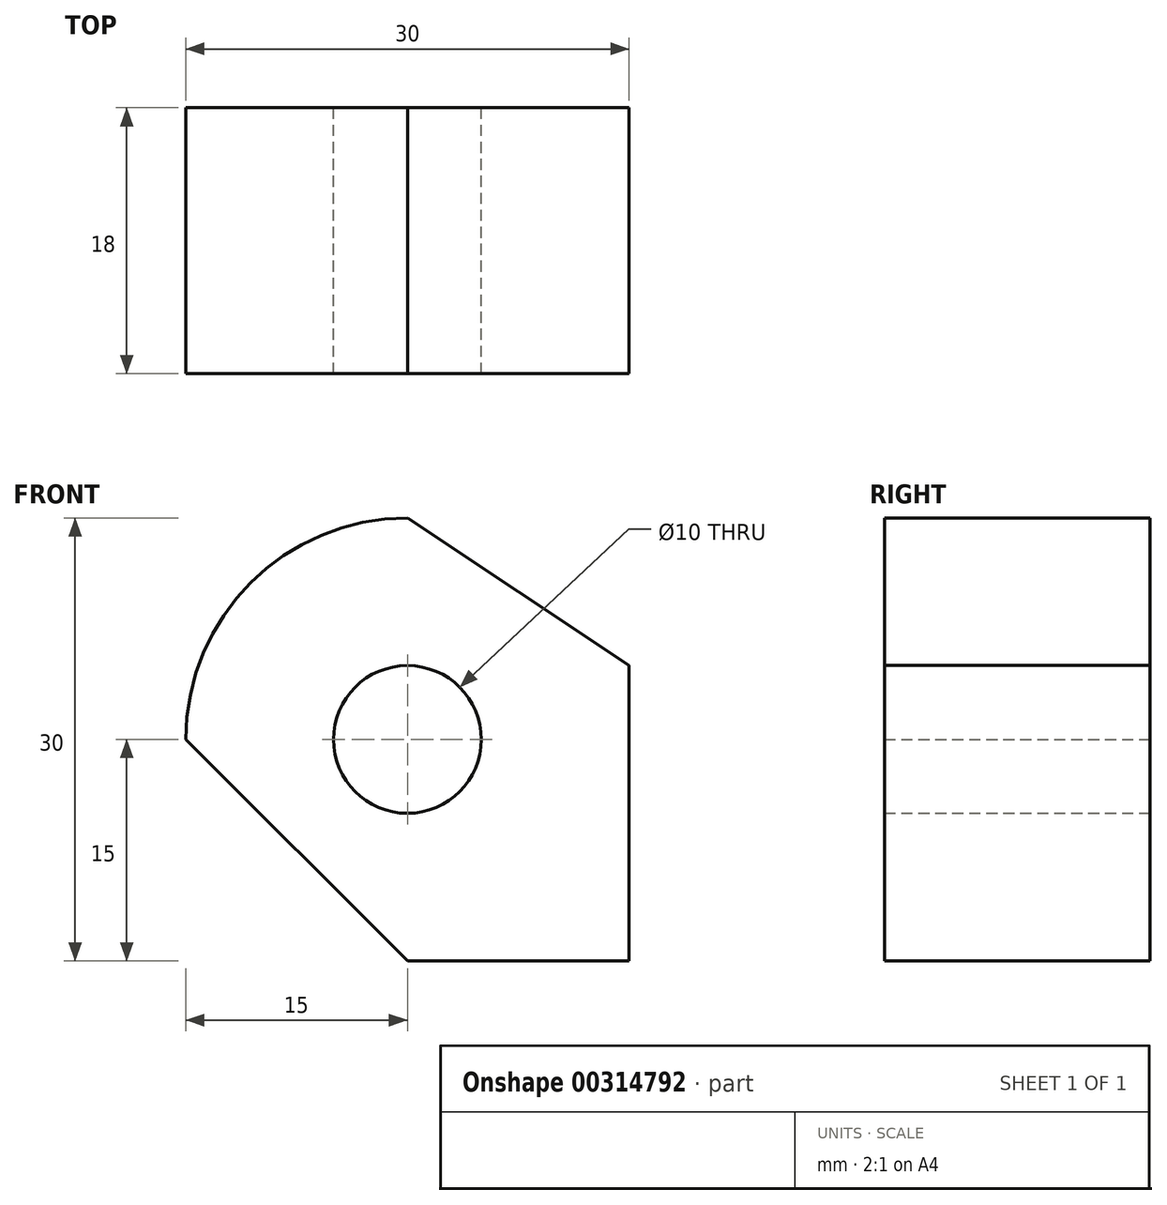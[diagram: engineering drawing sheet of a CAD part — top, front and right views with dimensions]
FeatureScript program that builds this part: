
annotation { "Feature Type Name" : "Feature", "Feature Type Description" : "" }
export const myFeature = defineFeature(function(context is Context, id is Id, definition is map)
    precondition{}
    {
        {
            var Q0;
            Q0=qCreatedBy(makeId("Front.planeOp"),FACE);
            var sketch = newSketch(context, id + "F0", { "sketchPlane" : qUnion([Q0])});
            skLineSegment(sketch, "E0.bottom", {"start": v(0, 0) * mm, "end": v(30, 0) * mm});
            skLineSegment(sketch, "E0.top", {"start": v(0, 30) * mm, "end": v(30, 30) * mm});
            skLineSegment(sketch, "E0.left", {"start": v(0, 0) * mm, "end": v(0, 30) * mm});
            skLineSegment(sketch, "E0.right", {"start": v(30, 0) * mm, "end": v(30, 30) * mm});
            skLineSegment(sketch, "E1", {"start": v(15, 30) * mm, "end": v(30, 20) * mm});
            skLineSegment(sketch, "E2", {"start": v(15, 0) * mm, "end": v(0, 15) * mm});
            skCircle(sketch, "E3", {"center": v(15, 15) * mm, "radius": 5 * mm});
            skSolve(sketch);
        }
        {
            var Q0;
            {var subQ4=sQuery(id+"F0.wireOp",EDGE,"E1");Q0=makeQuery(id+"F0.imprint","IMPRINT",FACE,{"disambiguationData":[TD([[makeQuery(id+"F0.imprint","IMPRINT",EDGE,{"derivedFrom":subQ4}),-1.0]])]});}
            extrude(context, id + "F1", {"entities" : qUnion([Q0]), "depth" : 18 * mm, "symmetric" : true});
        }
        {
            var Q0;
            Q0=makeQuery(id+"F1.opExtrude","SWEPT_EDGE",EDGE,{"disambiguationData":[OSD([sQuery(id+"F0.wireOp",EDGE,"E0.top"),sQuery(id+"F0.wireOp",EDGE,"E0.left")])]});
            fillet(context, id + "F2", {"entities" : qUnion([Q0]), "radius" : 15 * mm, "tangentPropagation" : true, "allowEdgeOverflow" : false});
        }
    });
